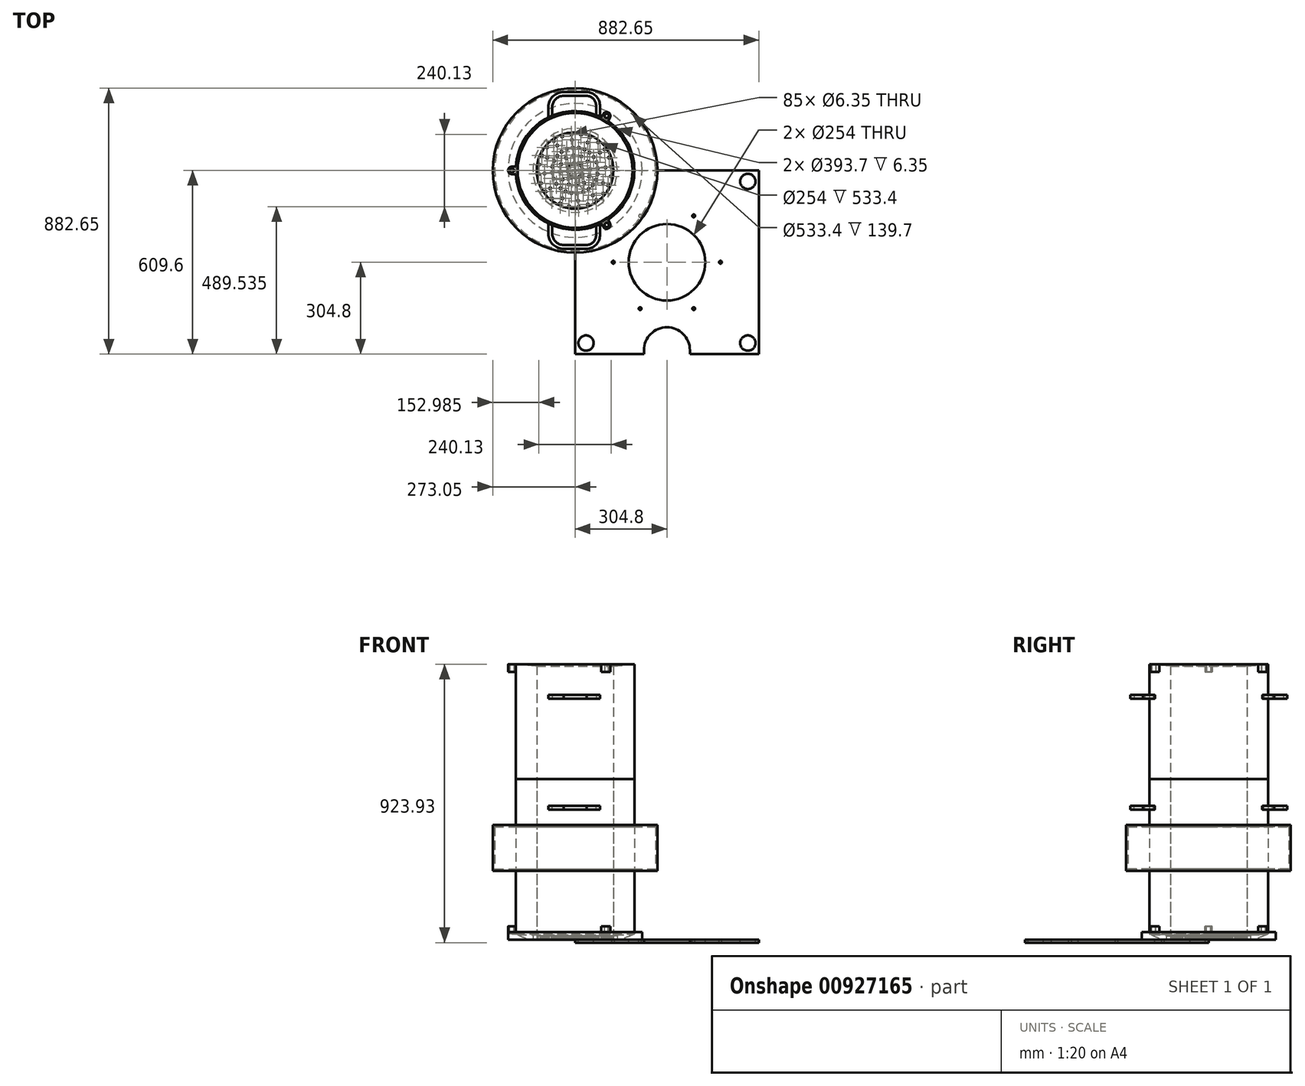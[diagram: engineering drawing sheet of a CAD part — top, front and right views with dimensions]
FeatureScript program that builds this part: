
annotation { "Feature Type Name" : "Feature", "Feature Type Description" : "" }
export const myFeature = defineFeature(function(context is Context, id is Id, definition is map)
    precondition{}
    {
        {
            var Q0;
            Q0=qCreatedBy(makeId("Top.planeOp"),FACE);
            var sketch = newSketch(context, id + "F0", { "sketchPlane" : qUnion([Q0])});
            skLineSegment(sketch, "E0.bottom", {"start": v(0, 0) * mm, "end": v(609.6, 0) * mm});
            skLineSegment(sketch, "E0.top", {"start": v(0, -609.6) * mm, "end": v(228.6, -609.6) * mm});
            skLineSegment(sketch, "E0.left", {"start": v(0, 0) * mm, "end": v(0, -609.6) * mm});
            skLineSegment(sketch, "E0.right", {"start": v(609.6, 0) * mm, "end": v(609.6, -609.6) * mm});
            skCircle(sketch, "E1", {"center": v(304.8, -304.8) * mm, "radius": 127 * mm});
            skPoint(sketch, "E1.centerSnap0", {"position": v(0, -304.8) * mm});
            skLineSegment(sketch, "E2", {"start": v(381, -609.6) * mm, "end": v(381, -596.9) * mm});
            skArc(sketch, "E3", {"start": v(381, -596.9) * mm, "mid": v(304.8, -520.7) * mm, "end": v(228.6, -596.9) * mm});
            skLineSegment(sketch, "E4.MirrorCS", {"start": v(228.6, -609.6) * mm, "end": v(228.6, -596.9) * mm});
            skPoint(sketch, "E5.orphan", {"position": v(381, -520.7) * mm});
            skPoint(sketch, "E6.orphan", {"position": v(228.6, -520.7) * mm});
            skLineSegment(sketch, "E7.trimOffspring", {"start": v(381, -609.6) * mm, "end": v(609.6, -609.6) * mm});
            skPoint(sketch, "E8.orphan", {"position": v(304.8, -520.7) * mm});
            skPoint(sketch, "E9.orphan", {"position": v(304.8, -609.6) * mm});
            skLineSegment(sketch, "E10", {"start": v(304.8, -304.8) * mm, "end": v(304.8, -520.7) * mm});
            skLineSegment(sketch, "E11", {"start": v(304.8, -304.8) * mm, "end": v(393.7, -458.78) * mm});
            skCircle(sketch, "E12", {"center": v(36.39, -573.21) * mm, "radius": 25.4 * mm});
            skCircle(sketch, "E13.MirrorC", {"center": v(573.21, -36.39) * mm, "radius": 25.4 * mm});
            skCircle(sketch, "E14.MirrorC", {"center": v(573.21, -573.21) * mm, "radius": 25.4 * mm});
            skCircle(sketch, "E15.MirrorC", {"center": v(36.39, -36.39) * mm, "radius": 25.4 * mm});
            skCircle(sketch, "E16", {"center": v(393.7, -458.78) * mm, "radius": 4.76 * mm});
            skCircle(sketch, "E17.1.0", {"center": v(482.6, -304.8) * mm, "radius": 4.76 * mm});
            skCircle(sketch, "E17.2.0", {"center": v(393.7, -150.82) * mm, "radius": 4.76 * mm});
            skCircle(sketch, "E17.3.0", {"center": v(215.9, -150.82) * mm, "radius": 4.76 * mm});
            skCircle(sketch, "E17.4.0", {"center": v(127, -304.8) * mm, "radius": 4.76 * mm});
            skCircle(sketch, "E17.5.0", {"center": v(215.9, -458.78) * mm, "radius": 4.76 * mm});
            skSolve(sketch);
        }
        {
            var Q0;
            Q0=makeQuery(id+"F0.imprint","IMPRINT",FACE,{"disambiguationData":[TD([[makeQuery(id+"F0.imprint","IMPRINT",EDGE,{"derivedFrom":sQuery(id+"F0.wireOp",EDGE,"E0.bottom")}),-1.0]])]});
            extrude(context, id + "F1", {"entities" : qUnion([Q0]), "oppositeDirection" : true, "depth" : 9.52 * mm, "offsetDistance" : 25.4 * mm});
        }
        {
            var Q0;
            Q0=qCreatedBy(makeId("Top.planeOp"),FACE);
            var sketch = newSketch(context, id + "F2", { "sketchPlane" : qUnion([Q0])});
            skCircle(sketch, "E18", {"center": v(0, 0) * mm, "radius": 139.7 * mm});
            skCircle(sketch, "E19", {"center": v(0, 0) * mm, "radius": 120.65 * mm});
            skLineSegment(sketch, "E20", {"start": v(-13.7, 139.03) * mm, "end": v(13.05, -139.09) * mm});
            skCircle(sketch, "E21", {"center": v(-11.87, 120.06) * mm, "radius": 3.18 * mm});
            skCircle(sketch, "E22.1.0", {"center": v(-70.31, 98.05) * mm, "radius": 3.18 * mm});
            skCircle(sketch, "E22.2.0", {"center": v(-109.91, 49.75) * mm, "radius": 3.18 * mm});
            skCircle(sketch, "E22.3.0", {"center": v(-120.06, -11.87) * mm, "radius": 3.18 * mm});
            skCircle(sketch, "E22.4.0", {"center": v(-98.05, -70.31) * mm, "radius": 3.18 * mm});
            skCircle(sketch, "E22.5.0", {"center": v(-49.75, -109.91) * mm, "radius": 3.18 * mm});
            skCircle(sketch, "E22.6.0", {"center": v(11.87, -120.06) * mm, "radius": 3.18 * mm});
            skCircle(sketch, "E22.7.0", {"center": v(70.31, -98.05) * mm, "radius": 3.18 * mm});
            skCircle(sketch, "E22.8.0", {"center": v(109.91, -49.75) * mm, "radius": 3.18 * mm});
            skCircle(sketch, "E22.9.0", {"center": v(120.06, 11.87) * mm, "radius": 3.18 * mm});
            skCircle(sketch, "E22.10.0", {"center": v(98.05, 70.31) * mm, "radius": 3.18 * mm});
            skCircle(sketch, "E22.11.0", {"center": v(49.75, 109.91) * mm, "radius": 3.18 * mm});
            skCircle(sketch, "E23", {"center": v(0, 0) * mm, "radius": 3.18 * mm});
            skCircle(sketch, "E24", {"center": v(-10.04, 101.1) * mm, "radius": 3.18 * mm});
            skCircle(sketch, "E25", {"center": v(-7.61, 75.82) * mm, "radius": 3.18 * mm});
            skCircle(sketch, "E26", {"center": v(-5.18, 50.54) * mm, "radius": 3.18 * mm});
            skCircle(sketch, "E27", {"center": v(-2.75, 25.25) * mm, "radius": 3.18 * mm});
            skCircle(sketch, "E28.1.0", {"center": v(-59.25, 82.54) * mm, "radius": 3.18 * mm});
            skCircle(sketch, "E28.1.1", {"center": v(-44.5, 61.85) * mm, "radius": 3.18 * mm});
            skCircle(sketch, "E28.1.2", {"center": v(-29.76, 41.17) * mm, "radius": 3.18 * mm});
            skCircle(sketch, "E28.1.3", {"center": v(-15, 20.5) * mm, "radius": 3.18 * mm});
            skCircle(sketch, "E28.2.0", {"center": v(-92.58, 41.85) * mm, "radius": 3.18 * mm});
            skCircle(sketch, "E28.2.1", {"center": v(-69.47, 31.32) * mm, "radius": 3.18 * mm});
            skCircle(sketch, "E28.2.2", {"center": v(-46.36, 20.78) * mm, "radius": 3.18 * mm});
            skCircle(sketch, "E28.2.3", {"center": v(-23.24, 10.24) * mm, "radius": 3.18 * mm});
            skCircle(sketch, "E28.3.0", {"center": v(-101.1, -10.04) * mm, "radius": 3.18 * mm});
            skCircle(sketch, "E28.3.1", {"center": v(-75.82, -7.61) * mm, "radius": 3.18 * mm});
            skCircle(sketch, "E28.3.2", {"center": v(-50.54, -5.18) * mm, "radius": 3.18 * mm});
            skCircle(sketch, "E28.3.3", {"center": v(-25.25, -2.75) * mm, "radius": 3.18 * mm});
            skCircle(sketch, "E28.4.0", {"center": v(-82.54, -59.25) * mm, "radius": 3.18 * mm});
            skCircle(sketch, "E28.4.1", {"center": v(-61.85, -44.5) * mm, "radius": 3.18 * mm});
            skCircle(sketch, "E28.4.2", {"center": v(-41.17, -29.76) * mm, "radius": 3.18 * mm});
            skCircle(sketch, "E28.4.3", {"center": v(-20.5, -15) * mm, "radius": 3.18 * mm});
            skCircle(sketch, "E28.5.0", {"center": v(-41.85, -92.58) * mm, "radius": 3.18 * mm});
            skCircle(sketch, "E28.5.1", {"center": v(-31.32, -69.47) * mm, "radius": 3.18 * mm});
            skCircle(sketch, "E28.5.2", {"center": v(-20.78, -46.36) * mm, "radius": 3.18 * mm});
            skCircle(sketch, "E28.5.3", {"center": v(-10.24, -23.24) * mm, "radius": 3.18 * mm});
            skCircle(sketch, "E28.6.0", {"center": v(10.04, -101.1) * mm, "radius": 3.18 * mm});
            skCircle(sketch, "E28.6.1", {"center": v(7.61, -75.82) * mm, "radius": 3.18 * mm});
            skCircle(sketch, "E28.6.2", {"center": v(5.18, -50.54) * mm, "radius": 3.18 * mm});
            skCircle(sketch, "E28.6.3", {"center": v(2.75, -25.25) * mm, "radius": 3.18 * mm});
            skCircle(sketch, "E28.7.0", {"center": v(59.25, -82.54) * mm, "radius": 3.18 * mm});
            skCircle(sketch, "E28.7.1", {"center": v(44.5, -61.85) * mm, "radius": 3.18 * mm});
            skCircle(sketch, "E28.7.2", {"center": v(29.76, -41.17) * mm, "radius": 3.18 * mm});
            skCircle(sketch, "E28.7.3", {"center": v(15, -20.5) * mm, "radius": 3.18 * mm});
            skCircle(sketch, "E28.8.0", {"center": v(92.58, -41.85) * mm, "radius": 3.18 * mm});
            skCircle(sketch, "E28.8.1", {"center": v(69.47, -31.32) * mm, "radius": 3.18 * mm});
            skCircle(sketch, "E28.8.2", {"center": v(46.36, -20.78) * mm, "radius": 3.18 * mm});
            skCircle(sketch, "E28.8.3", {"center": v(23.24, -10.24) * mm, "radius": 3.18 * mm});
            skCircle(sketch, "E28.9.0", {"center": v(101.1, 10.04) * mm, "radius": 3.18 * mm});
            skCircle(sketch, "E28.9.1", {"center": v(75.82, 7.61) * mm, "radius": 3.18 * mm});
            skCircle(sketch, "E28.9.2", {"center": v(50.54, 5.18) * mm, "radius": 3.18 * mm});
            skCircle(sketch, "E28.9.3", {"center": v(25.25, 2.75) * mm, "radius": 3.18 * mm});
            skCircle(sketch, "E28.10.0", {"center": v(82.54, 59.25) * mm, "radius": 3.18 * mm});
            skCircle(sketch, "E28.10.1", {"center": v(61.85, 44.5) * mm, "radius": 3.18 * mm});
            skCircle(sketch, "E28.10.2", {"center": v(41.17, 29.76) * mm, "radius": 3.18 * mm});
            skCircle(sketch, "E28.10.3", {"center": v(20.5, 15) * mm, "radius": 3.18 * mm});
            skCircle(sketch, "E28.11.0", {"center": v(41.85, 92.58) * mm, "radius": 3.18 * mm});
            skCircle(sketch, "E28.11.1", {"center": v(31.32, 69.47) * mm, "radius": 3.18 * mm});
            skCircle(sketch, "E28.11.2", {"center": v(20.78, 46.36) * mm, "radius": 3.18 * mm});
            skCircle(sketch, "E28.11.3", {"center": v(10.24, 23.24) * mm, "radius": 3.18 * mm});
            skCircle(sketch, "E29.1.0", {"center": v(-42.54, 112.9) * mm, "radius": 3.17 * mm});
            skCircle(sketch, "E29.1.1", {"center": v(-26.98, 71.26) * mm, "radius": 3.17 * mm});
            skCircle(sketch, "E30.1.3.0", {"center": v(-93.3, 76.5) * mm, "radius": 3.18 * mm});
            skCircle(sketch, "E30.2.3.0", {"center": v(-59, 48.23) * mm, "radius": 3.18 * mm});
            skCircle(sketch, "E30.1.5.0", {"center": v(-119.05, 19.61) * mm, "radius": 3.18 * mm});
            skCircle(sketch, "E30.2.5.0", {"center": v(-75.2, 12.27) * mm, "radius": 3.18 * mm});
            skCircle(sketch, "E30.1.7.0", {"center": v(-112.9, -42.54) * mm, "radius": 3.18 * mm});
            skCircle(sketch, "E30.2.7.0", {"center": v(-71.26, -26.98) * mm, "radius": 3.18 * mm});
            skCircle(sketch, "E30.1.9.0", {"center": v(-76.5, -93.3) * mm, "radius": 3.18 * mm});
            skCircle(sketch, "E30.2.9.0", {"center": v(-48.23, -59) * mm, "radius": 3.18 * mm});
            skCircle(sketch, "E30.1.11.0", {"center": v(-19.61, -119.05) * mm, "radius": 3.18 * mm});
            skCircle(sketch, "E30.2.11.0", {"center": v(-12.27, -75.2) * mm, "radius": 3.18 * mm});
            skCircle(sketch, "E30.1.13.0", {"center": v(42.54, -112.9) * mm, "radius": 3.18 * mm});
            skCircle(sketch, "E30.2.13.0", {"center": v(26.98, -71.26) * mm, "radius": 3.18 * mm});
            skCircle(sketch, "E30.1.15.0", {"center": v(93.3, -76.5) * mm, "radius": 3.18 * mm});
            skCircle(sketch, "E30.2.15.0", {"center": v(59, -48.23) * mm, "radius": 3.18 * mm});
            skCircle(sketch, "E30.1.17.0", {"center": v(119.05, -19.61) * mm, "radius": 3.18 * mm});
            skCircle(sketch, "E30.2.17.0", {"center": v(75.2, -12.27) * mm, "radius": 3.18 * mm});
            skCircle(sketch, "E30.1.19.0", {"center": v(112.9, 42.54) * mm, "radius": 3.18 * mm});
            skCircle(sketch, "E30.2.19.0", {"center": v(71.26, 26.98) * mm, "radius": 3.18 * mm});
            skCircle(sketch, "E30.1.21.0", {"center": v(76.5, 93.3) * mm, "radius": 3.18 * mm});
            skCircle(sketch, "E30.2.21.0", {"center": v(48.23, 59) * mm, "radius": 3.18 * mm});
            skCircle(sketch, "E30.1.23.0", {"center": v(19.61, 119.05) * mm, "radius": 3.18 * mm});
            skCircle(sketch, "E30.2.23.0", {"center": v(12.27, 75.2) * mm, "radius": 3.18 * mm});
            skSolve(sketch);
        }
        {
            var Q0;
            Q0 = qSketchRegion(id + "F2", true);
            var Q1;
            Q1=makeQuery(id+"F2.imprint","IMPRINT",FACE,{"disambiguationData":[TD([[makeQuery(id+"F2.imprint","IMPRINT",EDGE,{"derivedFrom":sQuery(id+"F2.wireOp",EDGE,"E28.1.0")}),-1.0]])]});
            var Q2;
            Q2=makeQuery(id+"F2.imprint","IMPRINT",FACE,{"disambiguationData":[TD([[makeQuery(id+"F2.imprint","IMPRINT",EDGE,{"derivedFrom":sQuery(id+"F2.wireOp",EDGE,"E28.7.0")}),-1.0]])]});
            extrude(context, id + "F3", {"entities" : qUnion([Q0, Q1, Q2]), "depth" : 12.7 * mm, "offsetDistance" : 25.4 * mm});
        }
        {
            var Q0;
            Q0=qCreatedBy(makeId("Right.planeOp"),FACE);
            var sketch = newSketch(context, id + "F4", { "sketchPlane" : qUnion([Q0])});
            skLineSegment(sketch, "E31", {"start": v(0, 0) * mm, "end": v(0, 139.7) * mm});
            skLineSegment(sketch, "E32", {"start": v(0, 0) * mm, "end": v(127, 0) * mm});
            skLineSegment(sketch, "E33", {"start": v(127, 0) * mm, "end": v(127, 533.4) * mm});
            skLineSegment(sketch, "E34", {"start": v(127, 533.4) * mm, "end": v(190.5, 533.4) * mm});
            skLineSegment(sketch, "E35", {"start": v(190.5, 914.4) * mm, "end": v(190.5, 17.26) * mm});
            skLineSegment(sketch, "E36", {"start": v(190.5, 533.4) * mm, "end": v(196.85, 533.4) * mm});
            skLineSegment(sketch, "E37", {"start": v(196.85, 533.4) * mm, "end": v(196.85, 18.98) * mm});
            skLineSegment(sketch, "E38", {"start": v(190.5, 17.26) * mm, "end": v(196.85, 18.98) * mm});
            skArc(sketch, "E39", {"start": v(127, 0) * mm, "mid": v(159.9, 4.4) * mm, "end": v(190.5, 17.26) * mm});
            skPoint(sketch, "E40.start.orphan", {"position": v(196.85, 0) * mm});
            skPoint(sketch, "E41.orphan", {"position": v(190.5, 0) * mm});
            skLineSegment(sketch, "E42", {"start": v(196.85, 18.98) * mm, "end": v(196.85, 0) * mm});
            skLineSegment(sketch, "E43", {"start": v(127, 0) * mm, "end": v(196.85, 0) * mm});
            skLineSegment(sketch, "E44", {"start": v(196.85, 0) * mm, "end": v(196.85, 914.4) * mm});
            skLineSegment(sketch, "E45", {"start": v(196.85, 914.4) * mm, "end": v(127, 914.4) * mm});
            skLineSegment(sketch, "E46", {"start": v(127, 914.4) * mm, "end": v(127, 533.4) * mm});
            skLineSegment(sketch, "E47", {"start": v(196.85, 0) * mm, "end": v(222.25, 0) * mm});
            skLineSegment(sketch, "E48", {"start": v(222.25, 0) * mm, "end": v(222.25, 25.4) * mm});
            skLineSegment(sketch, "E49", {"start": v(222.25, 25.4) * mm, "end": v(196.85, 25.4) * mm});
            skLineSegment(sketch, "E50", {"start": v(190.5, 914.4) * mm, "end": v(127, 908.42) * mm});
            skLineSegment(sketch, "E51", {"start": v(196.85, 228.6) * mm, "end": v(273.05, 228.6) * mm});
            skLineSegment(sketch, "E52", {"start": v(273.05, 228.6) * mm, "end": v(273.05, 381) * mm});
            skLineSegment(sketch, "E53", {"start": v(273.05, 381) * mm, "end": v(196.85, 381) * mm});
            skLineSegment(sketch, "E54", {"start": v(0, 0) * mm, "end": v(0, 50.8) * mm});
            skLineSegment(sketch, "E55.0", {"start": v(266.7, 374.65) * mm, "end": v(196.85, 374.65) * mm});
            skLineSegment(sketch, "E55.1", {"start": v(266.7, 234.95) * mm, "end": v(266.7, 374.65) * mm});
            skLineSegment(sketch, "E56.0", {"start": v(196.85, 234.95) * mm, "end": v(266.7, 234.95) * mm});
            skSolve(sketch);
        }
        {
            var Q0;
            Q0=makeQuery(id+"F4.imprint","IMPRINT",FACE,{"disambiguationData":[TD([[makeQuery(id+"F4.imprint","IMPRINT",EDGE,{"derivedFrom":sQuery(id+"F4.wireOp",EDGE,"E33")}),-1.0]])]});
            var Q1;
            {var subQ1=sQuery(id+"F4.wireOp",EDGE,"E36");Q1=makeQuery(id+"F4.imprint","IMPRINT",FACE,{"disambiguationData":[TD([[makeQuery(id+"F4.imprint","IMPRINT",EDGE,{"derivedFrom":subQ1}),-1.0]])]});}
            var Q2;
            Q2=sQuery(id+"F4.wireOp",EDGE,"E31");
            revolve(context, id + "F5", {"surfaceOperationType" : NewSurfaceOperationType.NEW, "entities" : qUnion([Q0, Q1]), "axis" : qUnion([Q2]), "revolveType" : RevolveType.FULL});
        }
        {
            var Q0;
            Q0=makeQuery(id+"F5.opRevolve","SWEPT_FACE",FACE,{"disambiguationData":[OSD([sQuery(id+"F4.wireOp",EDGE,"E34"),sQuery(id+"F4.wireOp",EDGE,"E36")])]});
            var sketch = newSketch(context, id + "F6", { "sketchPlane" : qUnion([Q0])});
            skArc(sketch, "E57", {"start": v(-209.44, 12.6) * mm, "mid": v(-222.03, 0) * mm, "end": v(-209.44, -12.6) * mm});
            skLineSegment(sketch, "E58", {"start": v(-209.44, 0) * mm, "end": v(-196.85, 0) * mm});
            skLineSegment(sketch, "E59", {"start": v(-209.44, -12.6) * mm, "end": v(-196.45, -12.6) * mm});
            skLineSegment(sketch, "E60.MirrorCS", {"start": v(-209.44, 12.6) * mm, "end": v(-196.45, 12.6) * mm});
            skPoint(sketch, "E61.center.orphan", {"position": v(-203.15, 0) * mm});
            skCircle(sketch, "E62", {"center": v(-209.44, 0) * mm, "radius": 7.14 * mm});
            skArc(sketch, "E63.1.0", {"start": v(93.82, -187.68) * mm, "mid": v(111.02, -192.29) * mm, "end": v(115.63, -175.09) * mm});
            skCircle(sketch, "E63.1.1", {"center": v(104.72, -181.38) * mm, "radius": 7.14 * mm});
            skLineSegment(sketch, "E63.1.2", {"start": v(115.63, -175.09) * mm, "end": v(109.13, -163.83) * mm});
            skLineSegment(sketch, "E63.1.3", {"start": v(93.82, -187.68) * mm, "end": v(87.32, -176.42) * mm});
            skArc(sketch, "E63.2.0", {"start": v(115.63, 175.09) * mm, "mid": v(111.02, 192.29) * mm, "end": v(93.82, 187.68) * mm});
            skCircle(sketch, "E63.2.1", {"center": v(104.72, 181.38) * mm, "radius": 7.14 * mm});
            skLineSegment(sketch, "E63.2.2", {"start": v(93.82, 187.68) * mm, "end": v(87.32, 176.42) * mm});
            skLineSegment(sketch, "E63.2.3", {"start": v(115.63, 175.09) * mm, "end": v(109.13, 163.83) * mm});
            skPoint(sketch, "E63.center", {"position": v(0, 0) * mm});
            skLineSegment(sketch, "E64", {"start": v(0, 0) * mm, "end": v(40.58, 0) * mm});
            skLineSegment(sketch, "E65", {"start": v(0, 0) * mm, "end": v(0, 196.85) * mm});
            skLineSegment(sketch, "E66", {"start": v(69.85, 184.04) * mm, "end": v(69.85, 216.95) * mm});
            skArc(sketch, "E67", {"start": v(69.85, 216.95) * mm, "mid": v(59.96, 238.56) * mm, "end": v(37.99, 247.65) * mm});
            skPoint(sketch, "E68.orphan", {"position": v(69.85, 254) * mm});
            skPoint(sketch, "E69.orphan", {"position": v(69.85, 242.8) * mm});
            skPoint(sketch, "E70.orphan", {"position": v(69.85, 213.42) * mm});
            skLineSegment(sketch, "E71.MirrorCS", {"start": v(38.04, 247.65) * mm, "end": v(-38.1, 247.65) * mm});
            skArc(sketch, "E72.MirrorCS", {"start": v(-76.1, 210.76) * mm, "mid": v(-64.33, 236.72) * mm, "end": v(-38, 247.65) * mm});
            skLineSegment(sketch, "E73.MirrorCS", {"start": v(-76.1, 181.55) * mm, "end": v(-76.1, 211.05) * mm});
            skLineSegment(sketch, "E74.0", {"start": v(-88.8, 175.46) * mm, "end": v(-88.8, 211.2) * mm});
            skLineSegment(sketch, "E74.1", {"start": v(82.55, 178.7) * mm, "end": v(82.55, 217.26) * mm});
            skArc(sketch, "E74.2", {"start": v(82.55, 217.26) * mm, "mid": v(68.89, 247.6) * mm, "end": v(38.15, 260.35) * mm});
            skLineSegment(sketch, "E74.3", {"start": v(38.15, 260.35) * mm, "end": v(-38.15, 260.35) * mm});
            skArc(sketch, "E74.4", {"start": v(-88.8, 211.2) * mm, "mid": v(-73.2, 245.8) * mm, "end": v(-38.15, 260.35) * mm});
            skCircle(sketch, "E75", {"center": v(0, 0) * mm, "radius": 196.85 * mm});
            skPoint(sketch, "E76.orphan", {"position": v(69.85, 184.04) * mm});
            skLineSegment(sketch, "E77.MirrorCS", {"start": v(38.15, -260.35) * mm, "end": v(-38.15, -260.35) * mm});
            skLineSegment(sketch, "E78.MirrorCS", {"start": v(38.04, -247.65) * mm, "end": v(-38.1, -247.65) * mm});
            skArc(sketch, "E79.MirrorCS", {"start": v(-88.8, -211.2) * mm, "mid": v(-73.2, -245.8) * mm, "end": v(-38.15, -260.35) * mm});
            skArc(sketch, "E80.MirrorCS", {"start": v(-76.1, -210.76) * mm, "mid": v(-64.33, -236.72) * mm, "end": v(-38, -247.65) * mm});
            skLineSegment(sketch, "E81.MirrorCS", {"start": v(-76.1, -181.55) * mm, "end": v(-76.1, -211.05) * mm});
            skLineSegment(sketch, "E82.MirrorCS", {"start": v(-88.8, -175.46) * mm, "end": v(-88.8, -211.2) * mm});
            skArc(sketch, "E83.MirrorCS", {"start": v(82.55, -217.26) * mm, "mid": v(68.89, -247.6) * mm, "end": v(38.15, -260.35) * mm});
            skArc(sketch, "E84.MirrorCS", {"start": v(69.85, -216.95) * mm, "mid": v(59.96, -238.56) * mm, "end": v(37.99, -247.65) * mm});
            skLineSegment(sketch, "E85.MirrorCS", {"start": v(82.55, -178.7) * mm, "end": v(82.55, -217.26) * mm});
            skLineSegment(sketch, "E86.MirrorCS", {"start": v(69.85, -184.04) * mm, "end": v(69.85, -216.95) * mm});
            skLineSegment(sketch, "E87", {"start": v(0, 0) * mm, "end": v(-228.28, 0) * mm});
            skSolve(sketch);
        }
        {
            var Q0;
            {var subQ1=sQuery(id+"F6.wireOp",EDGE,"E63.1.0");Q0=makeQuery(id+"F6.imprint","IMPRINT",FACE,{"disambiguationData":[TD([[makeQuery(id+"F6.imprint","IMPRINT",EDGE,{"derivedFrom":subQ1}),1.0]])]});}
            var Q1;
            {var subQ1=sQuery(id+"F6.wireOp",EDGE,"E57");Q1=makeQuery(id+"F6.imprint","IMPRINT",FACE,{"disambiguationData":[TD([[makeQuery(id+"F6.imprint","IMPRINT",EDGE,{"derivedFrom":subQ1}),1.0]])]});}
            var Q2;
            {var subQ1=sQuery(id+"F6.wireOp",EDGE,"E63.2.0");Q2=makeQuery(id+"F6.imprint","IMPRINT",FACE,{"disambiguationData":[TD([[makeQuery(id+"F6.imprint","IMPRINT",EDGE,{"derivedFrom":subQ1}),1.0]])]});}
            extrude(context, id + "F7", {"entities" : qUnion([Q0, Q1, Q2]), "operationType" : NewBodyOperationType.ADD, "oppositeDirection" : true, "depth" : 514.35 * mm, "offsetDistance" : 25.4 * mm, "hasSecondDirection" : true, "secondDirectionOppositeDirection" : true, "secondDirectionDepth" : 488.95 * mm});
        }
        {
            var Q0;
            {var subQ15=sQuery(id+"F6.wireOp",EDGE,"E66");Q0=makeQuery(id+"F6.imprint","IMPRINT",FACE,{"disambiguationData":[TD([[makeQuery(id+"F6.imprint","IMPRINT",EDGE,{"derivedFrom":subQ15}),-1.0]])]});}
            var Q1;
            Q1=makeQuery(id+"F6.imprint","IMPRINT",FACE,{"disambiguationData":[TD([[makeQuery(id+"F6.imprint","IMPRINT",EDGE,{"derivedFrom":sQuery(id+"F6.wireOp",EDGE,"E77.MirrorCS")}),-1.0]])]});
            extrude(context, id + "F8", {"entities" : qUnion([Q0, Q1]), "operationType" : NewBodyOperationType.ADD, "oppositeDirection" : true, "depth" : 101.6 * mm, "offsetDistance" : 25.4 * mm, "hasSecondDirection" : true, "secondDirectionOppositeDirection" : true, "secondDirectionDepth" : 88.9 * mm});
        }
        {
            var Q0;
            Q0=makeQuery(id+"F4.imprint","IMPRINT",FACE,{"disambiguationData":[TD([[makeQuery(id+"F4.imprint","IMPRINT",EDGE,{"derivedFrom":sQuery(id+"F4.wireOp",EDGE,"E33")}),-1.0]])]});
            var Q1;
            {var subQ1=sQuery(id+"F4.wireOp",EDGE,"E36");Q1=makeQuery(id+"F4.imprint","IMPRINT",FACE,{"disambiguationData":[TD([[makeQuery(id+"F4.imprint","IMPRINT",EDGE,{"derivedFrom":subQ1}),-1.0]])]});}
            var Q2;
            {var subQ0=sQuery(id+"F4.wireOp",EDGE,"E34");Q2=makeQuery(id+"F4.imprint","IMPRINT",FACE,{"disambiguationData":[TD([[makeQuery(id+"F4.imprint","IMPRINT",EDGE,{"derivedFrom":subQ0}),1.0]])]});}
            var Q3;
            Q3=makeQuery(id+"F5.opRevolve","SWEPT_FACE",FACE,{"disambiguationData":[OSD([sQuery(id+"F4.wireOp",EDGE,"E45")])]});
            var Q4;
            {var subQ0=sQuery(id+"F4.wireOp",EDGE,"E36");Q4=makeQuery(id+"F4.imprint","IMPRINT",FACE,{"disambiguationData":[TD([[makeQuery(id+"F4.imprint","IMPRINT",EDGE,{"derivedFrom":subQ0}),1.0]])]});}
            var Q5;
            Q5=makeQuery(id+"F4.imprint","IMPRINT",FACE,{"disambiguationData":[TD([[makeQuery(id+"F4.imprint","IMPRINT",EDGE,{"derivedFrom":sQuery(id+"F4.wireOp",EDGE,"E38")}),-1.0]])]});
            var Q6;
            {var subQ0=sQuery(id+"F4.wireOp",EDGE,"E42");Q6=makeQuery(id+"F4.imprint","IMPRINT",FACE,{"disambiguationData":[TD([[makeQuery(id+"F4.imprint","IMPRINT",EDGE,{"derivedFrom":subQ0}),1.0]])]});}
            var Q7;
            Q7=sQuery(id+"F4.wireOp",EDGE,"E31");
            revolve(context, id + "F9", {"surfaceOperationType" : NewSurfaceOperationType.NEW, "entities" : qUnion([Q0, Q1, Q2, Q3, Q4, Q5, Q6]), "axis" : qUnion([Q7]), "revolveType" : RevolveType.FULL});
        }
        {
            var Q0;
            {var subQ9=sQuery(id+"F6.wireOp",EDGE,"E66");Q0=makeQuery(id+"F6.imprint","IMPRINT",FACE,{"disambiguationData":[TD([[makeQuery(id+"F6.imprint","IMPRINT",EDGE,{"derivedFrom":subQ9}),-1.0]])]});}
            var Q1;
            Q1=makeQuery(id+"F6.imprint","IMPRINT",FACE,{"disambiguationData":[TD([[makeQuery(id+"F6.imprint","IMPRINT",EDGE,{"derivedFrom":sQuery(id+"F6.wireOp",EDGE,"E77.MirrorCS")}),-1.0]])]});
            extrude(context, id + "F10", {"entities" : qUnion([Q0, Q1]), "operationType" : NewBodyOperationType.ADD, "depth" : 279.4 * mm, "offsetDistance" : 25.4 * mm, "hasSecondDirection" : true, "secondDirectionOppositeDirection" : false, "secondDirectionDepth" : 266.7 * mm});
        }
        {
            var Q0;
            {var subQ4=sQuery(id+"F6.wireOp",EDGE,"E59");Q0=makeQuery(id+"F6.imprint","IMPRINT",FACE,{"disambiguationData":[TD([[makeQuery(id+"F6.imprint","IMPRINT",EDGE,{"derivedFrom":subQ4}),1.0]])]});}
            var Q1;
            {var subQ1=sQuery(id+"F6.wireOp",EDGE,"E60.MirrorCS");Q1=makeQuery(id+"F6.imprint","IMPRINT",FACE,{"disambiguationData":[TD([[makeQuery(id+"F6.imprint","IMPRINT",EDGE,{"derivedFrom":subQ1}),-1.0]])]});}
            var Q2;
            Q2=makeQuery(id+"F6.imprint","IMPRINT",FACE,{"disambiguationData":[TD([[makeQuery(id+"F6.imprint","IMPRINT",EDGE,{"derivedFrom":sQuery(id+"F6.wireOp",EDGE,"E63.2.0")}),1.0]])]});
            var Q3;
            Q3=makeQuery(id+"F6.imprint","IMPRINT",FACE,{"disambiguationData":[TD([[makeQuery(id+"F6.imprint","IMPRINT",EDGE,{"derivedFrom":sQuery(id+"F6.wireOp",EDGE,"E63.1.0")}),1.0]])]});
            var Q4;
            Q4=makeQuery(id+"F9.opRevolve","SWEPT_FACE",FACE,{"disambiguationData":[OSD([sQuery(id+"F4.wireOp",EDGE,"E45")])]});
            extrude(context, id + "F11", {"entities" : qUnion([Q0, Q1, Q2, Q3]), "operationType" : NewBodyOperationType.ADD, "endBound" : BoundingType.UP_TO_SURFACE, "depth" : 381 * mm, "endBoundEntityFace" : qUnion([Q4]), "offsetDistance" : 25.4 * mm, "hasSecondDirection" : true, "secondDirectionOppositeDirection" : false, "secondDirectionDepth" : 355.6 * mm});
        }
        {
            var Q0;
            {var subQ3=sQuery(id+"F4.wireOp",EDGE,"E51");Q0=makeQuery(id+"F4.imprint","IMPRINT",FACE,{"disambiguationData":[TD([[makeQuery(id+"F4.imprint","IMPRINT",EDGE,{"derivedFrom":subQ3}),1.0]])]});}
            var Q1;
            Q1=sQuery(id+"F4.wireOp",EDGE,"E31");
            revolve(context, id + "F12", {"surfaceOperationType" : NewSurfaceOperationType.NEW, "entities" : qUnion([Q0]), "axis" : qUnion([Q1]), "revolveType" : RevolveType.FULL});
        }
    });
